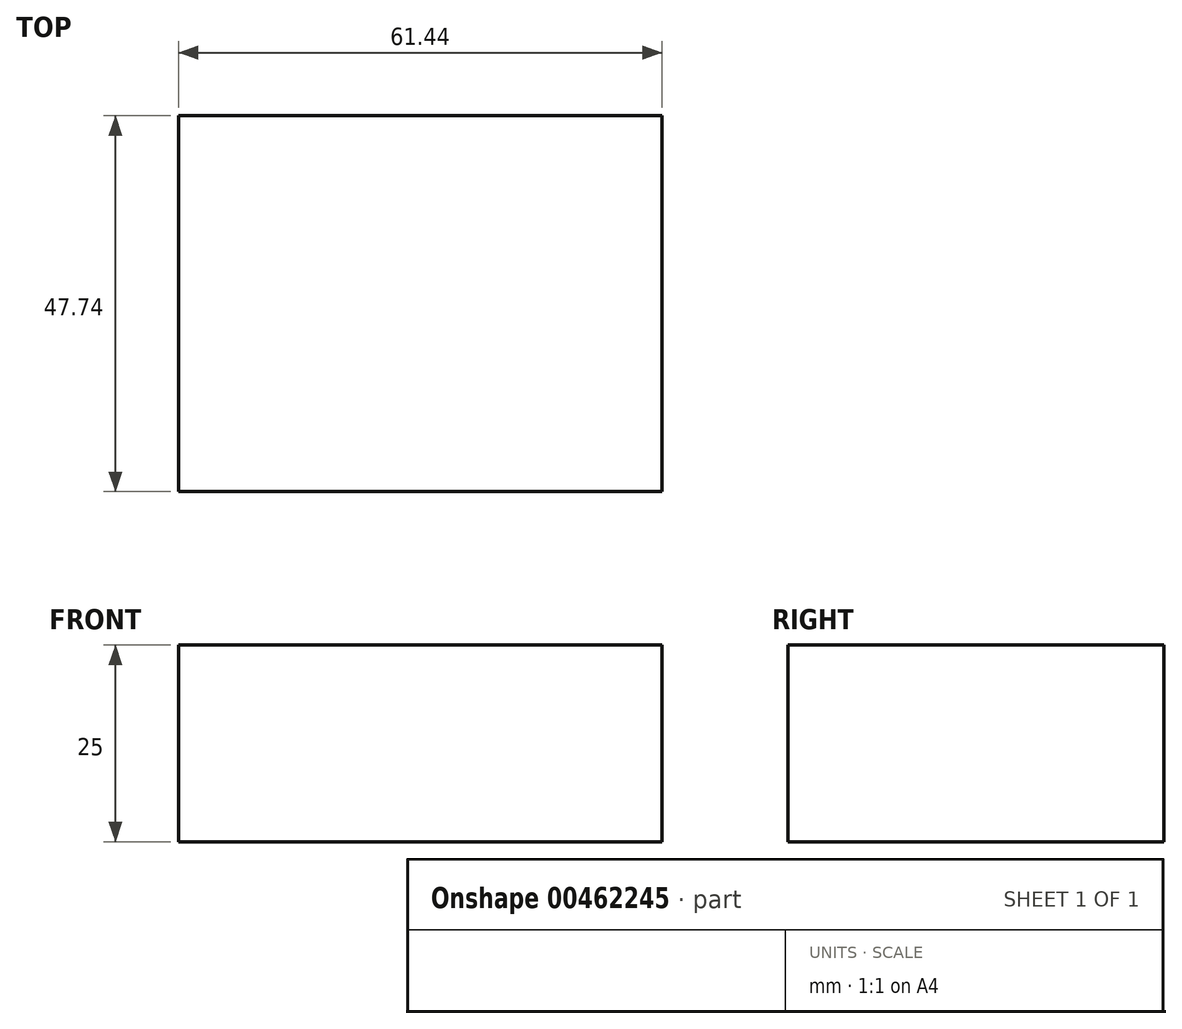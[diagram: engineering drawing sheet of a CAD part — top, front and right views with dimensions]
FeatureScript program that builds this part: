
annotation { "Feature Type Name" : "Feature", "Feature Type Description" : "" }
export const myFeature = defineFeature(function(context is Context, id is Id, definition is map)
    precondition{}
    {
        {
            var Q0;
            Q0=qCreatedBy(makeId("Top.planeOp"),FACE);
            var sketch = newSketch(context, id + "F0", { "sketchPlane" : qUnion([Q0])});
            skLineSegment(sketch, "E0.bottom", {"start": v(0, 0) * mm, "end": v(61.44, 0) * mm});
            skLineSegment(sketch, "E0.top", {"start": v(0, -47.74) * mm, "end": v(61.44, -47.74) * mm});
            skLineSegment(sketch, "E0.left", {"start": v(0, 0) * mm, "end": v(0, -47.74) * mm});
            skLineSegment(sketch, "E0.right", {"start": v(61.44, 0) * mm, "end": v(61.44, -47.74) * mm});
            skSolve(sketch);
        }
        {
            var Q0;
            Q0 = qSketchRegion(id + "F0", true);
            extrude(context, id + "F1", {"entities" : qUnion([Q0]), "depth" : 25 * mm});
        }
    });
